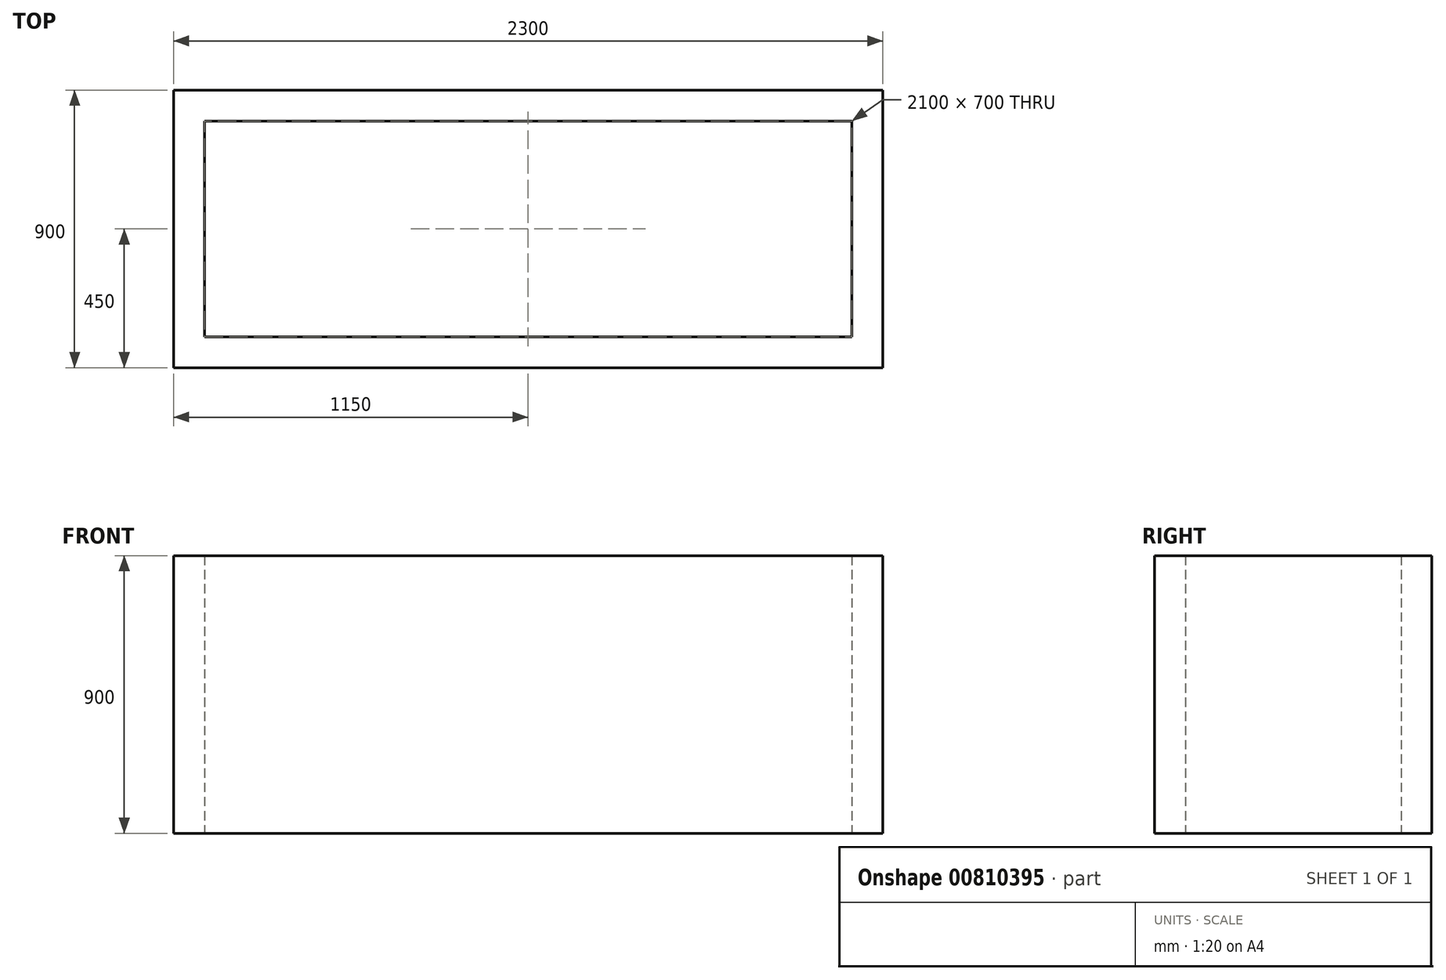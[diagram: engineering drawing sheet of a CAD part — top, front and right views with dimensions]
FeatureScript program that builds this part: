
annotation { "Feature Type Name" : "Feature", "Feature Type Description" : "" }
export const myFeature = defineFeature(function(context is Context, id is Id, definition is map)
    precondition{}
    {
        {
            var Q0;
            Q0=qCreatedBy(makeId("Top.planeOp"),FACE);
            var sketch = newSketch(context, id + "F0", { "sketchPlane" : qUnion([Q0])});
            skLineSegment(sketch, "E0.bottom", {"start": v(-1050, 350) * mm, "end": v(1050, 350) * mm});
            skLineSegment(sketch, "E0.top", {"start": v(-1050, -350) * mm, "end": v(1050, -350) * mm});
            skLineSegment(sketch, "E0.left", {"start": v(-1050, 350) * mm, "end": v(-1050, -350) * mm});
            skLineSegment(sketch, "E0.right", {"start": v(1050, 350) * mm, "end": v(1050, -350) * mm});
            skLineSegment(sketch, "E1.0", {"start": v(-1150, 450) * mm, "end": v(1150, 450) * mm});
            skLineSegment(sketch, "E1.1", {"start": v(-1150, 450) * mm, "end": v(-1150, -450) * mm});
            skLineSegment(sketch, "E1.2", {"start": v(-1150, -450) * mm, "end": v(1150, -450) * mm});
            skLineSegment(sketch, "E1.3", {"start": v(1150, 450) * mm, "end": v(1150, -450) * mm});
            skSolve(sketch);
        }
        {
            var Q0;
            Q0=makeQuery(id+"F0.imprint","IMPRINT",FACE,{"disambiguationData":[TD([[makeQuery(id+"F0.imprint","IMPRINT",EDGE,{"derivedFrom":sQuery(id+"F0.wireOp",EDGE,"E0.bottom")}),1.0]])]});
            extrude(context, id + "F1", {"entities" : qUnion([Q0]), "endBound" : BoundingType.SYMMETRIC, "depth" : 900 * mm, "offsetDistance" : 25 * mm});
        }
    });
